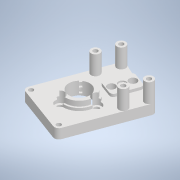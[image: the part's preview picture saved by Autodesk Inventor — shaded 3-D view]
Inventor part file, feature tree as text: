
AUTODESK INVENTOR PART (.ipt)
format: ipt  version: 2022 (Build 260153070, 153G)  size: 380,416 bytes
history: native  units: mm
features: reference x21, extrude x12, sketch x12, other x7, projected_geometry x6
ambient origin geometry x8: Origin, YZ Plane, XZ Plane, XY Plane, X Axis, Y Axis, Z Axis, Center Point
bodies: Solid1 (feature_tree)
feature tree (58):
  extrude  "Extrusion1"  Depth=3.0mm
  extrude  "Extrusion2"  Depth=30.0mm
  extrude  "Extrusion3"  Depth=3.0mm TaperAngle=0.0deg
  extrude  "Extrusion4"  Depth=6.15mm
  extrude  "Extrusion5"  Depth=1.6mm TaperAngle=0.0deg
  extrude  "Extrusion6"  Depth=0.35mm
  extrude  "Extrusion7"  Depth=1.6mm TaperAngle=0.0deg
  extrude  "Extrusion8"  Depth=3.0mm TaperAngle=0.0deg
  extrude  "Extrusion9"  Depth=3.0mm
  extrude  "Extrusion10"  Depth=6.5mm
  extrude  "Extrusion11"  Depth=5.5mm
  extrude  "Extrusion12"  Depth=2.0mm
  sketch  "Sketch1"  dims[d0=3.0mm d1=2.7mm]
  reference  "Reference1"
  reference  "Reference2"
  reference  "Reference3"
  reference  "Reference4"
  reference  "Reference5"
  reference  "Reference6"
  reference  "Reference9"
  reference  "Reference10"
  reference  "Reference11"
  reference  "Reference12"
  reference  "Reference13"
  reference  "Reference14"
  sketch  "Sketch2"  dims[d2=2.7mm d3=30.0mm]
  reference  "Reference15"
  reference  "Reference16"
  reference  "Reference17"
  sketch  "Sketch3"  dims[d4=1.25mm d5=3.0mm d6=0.0mm]
  sketch  "Sketch4"  dims[d7=2.5mm d8=6.15mm]
  sketch  "Sketch5"  dims[d10=1.25mm d11=1.6mm d12=0.0mm]
  reference  "Reference18"
  reference  "Reference19"
  reference  "Reference20"
  sketch  "Sketch6"  dims[d13=1.25mm d14=0.35mm]
  sketch  "Sketch7"  dims[d15=19.0mm d16=1.6mm d17=0.0mm]
  reference  "Reference21"
  reference  "Reference22"
  reference  "Reference23"
  sketch  "Sketch8"  dims[d18=16.95mm d19=3.0mm d20=0.0mm]
  sketch  "Sketch9"  dims[d21=3.0mm d22=0.0mm d23=5.75mm]
  sketch  "Sketch10"  dims[d24=6.5mm d25=0.0mm d26=0.4mm]
  projected_geometry  "Projected Loop1"
  projected_geometry  "Projected Loop2"
  projected_geometry  "Projected Loop3"
  projected_geometry  "Projected Loop4"
  sketch  "Sketch11"  dims[d27=5.5mm d28=5.5mm]
  projected_geometry  "Projected Loop5"
  sketch  "Sketch12"  dims[d29=2.7mm d30=2.0mm d31=1.6mm d32=0.0mm d33=4.6mm d34=4.6mm d35=3.6mm d36=0.0mm d37=2.3mm d38=10.0mm d39=0.0mm d40=11.32mm d41=0.0mm d42=1.3mm d43=0.0mm d44=1.25mm d45=0.0mm]
  projected_geometry  "Projected Loop6"
  other  "<userpath> laptop\Desktop\SumoBot\sumobotLIDAR\AssemblyV4\AsemblyV4.iam"
  other  "AsemblyV4.iam"
  other  "AS5600HolderV2:1"
  other  "SRM-12-06A:1"
  other  "MOTOR:1"
  other  "Spur Gears:1"
  other  "Spur Gear1:1"
